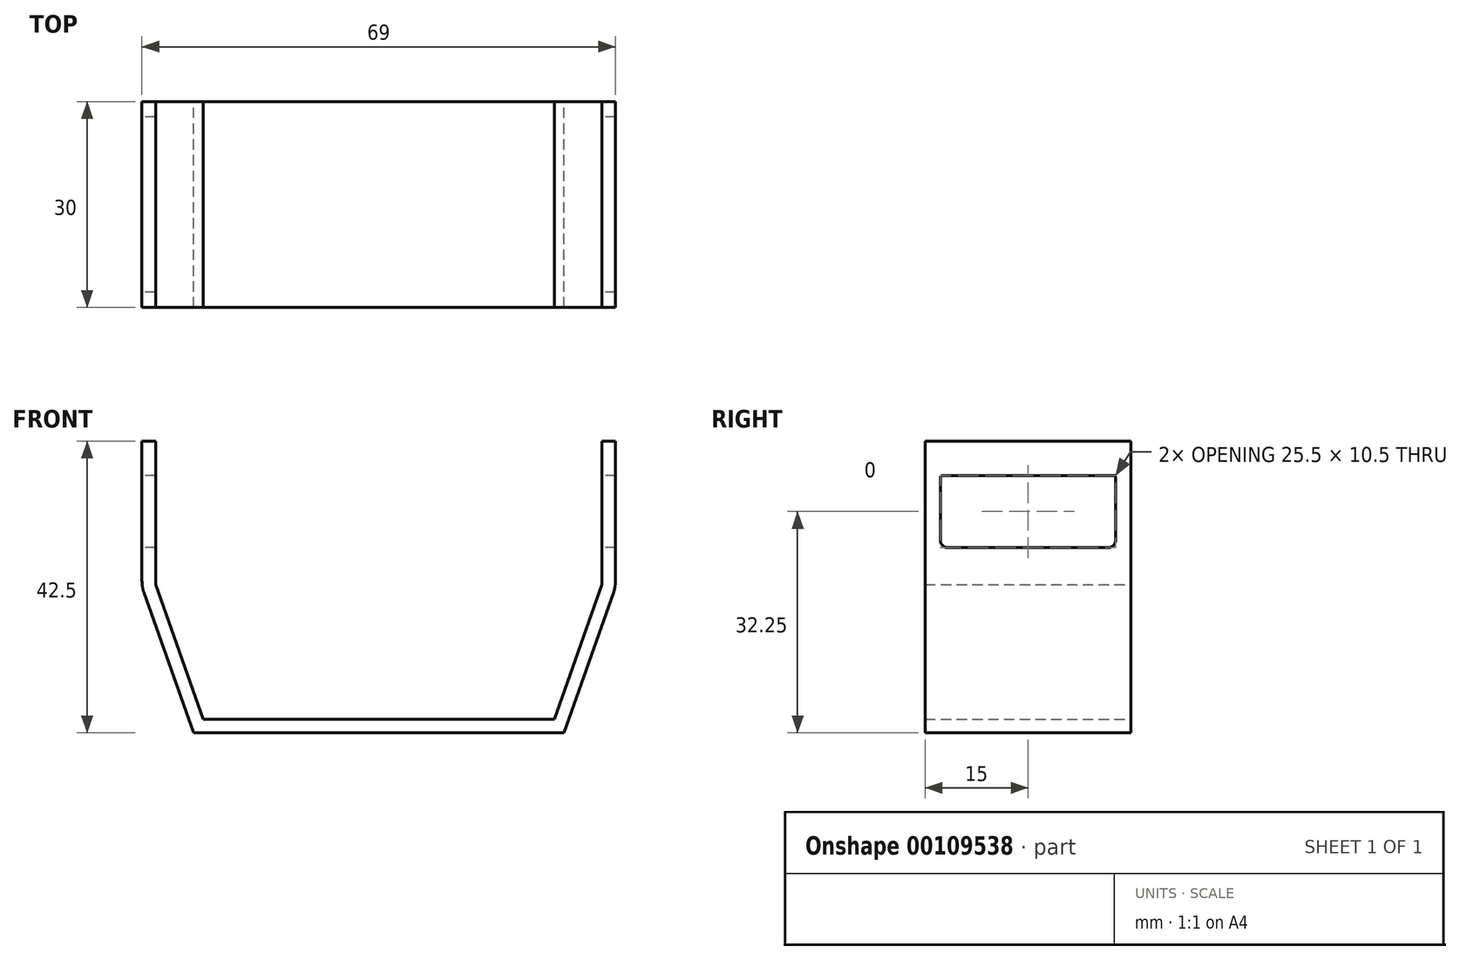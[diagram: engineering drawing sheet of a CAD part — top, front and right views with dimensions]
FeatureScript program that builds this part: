
annotation { "Feature Type Name" : "Feature", "Feature Type Description" : "" }
export const myFeature = defineFeature(function(context is Context, id is Id, definition is map)
    precondition{}
    {
        {
            var Q0;
            Q0=qCreatedBy(makeId("Front.planeOp"),FACE);
            var sketch = newSketch(context, id + "F0", { "sketchPlane" : qUnion([Q0])});
            skLineSegment(sketch, "E0", {"start": v(34.5, 0) * mm, "end": v(34.5, 21.25) * mm, "construction": true});
            skLineSegment(sketch, "E1", {"start": v(0, 0) * mm, "end": v(27, 0) * mm});
            skLineSegment(sketch, "E2", {"start": v(0, 0) * mm, "end": v(0, -5.67) * mm, "construction": true});
            skLineSegment(sketch, "E3", {"start": v(0, -5.67) * mm, "end": v(34.5, -5.67) * mm, "construction": true});
            skLineSegment(sketch, "E4", {"start": v(34.5, -5.67) * mm, "end": v(34.5, 0) * mm, "construction": true});
            skLineSegment(sketch, "E5", {"start": v(27, 0) * mm, "end": v(34.21, 20.44) * mm});
            skLineSegment(sketch, "E6", {"start": v(34.5, 22.1) * mm, "end": v(34.5, 42.5) * mm});
            skPoint(sketch, "E7.visualSharp", {"position": v(34.5, 21.25) * mm});
            skArc(sketch, "E7.filletArc", {"start": v(34.21, 20.44) * mm, "mid": v(34.43, 21.26) * mm, "end": v(34.5, 22.1) * mm});
            skLineSegment(sketch, "E8.0", {"start": v(32.5, 21.6) * mm, "end": v(32.5, 42.5) * mm});
            skLineSegment(sketch, "E8.1", {"start": v(25.58, 2) * mm, "end": v(32.5, 21.6) * mm});
            skLineSegment(sketch, "E8.2", {"start": v(0, 2) * mm, "end": v(25.58, 2) * mm});
            skLineSegment(sketch, "E9", {"start": v(32.5, 42.5) * mm, "end": v(34.5, 42.5) * mm});
            skArc(sketch, "E10.MirrorCS", {"start": v(-34.21, 20.44) * mm, "mid": v(-34.43, 21.26) * mm, "end": v(-34.5, 22.1) * mm});
            skLineSegment(sketch, "E11.MirrorCS", {"start": v(-32.5, 42.5) * mm, "end": v(-34.5, 42.5) * mm});
            skPoint(sketch, "E12.MirrorP", {"position": v(-34.5, 21.25) * mm});
            skLineSegment(sketch, "E13.MirrorCS", {"start": v(-25.58, 2) * mm, "end": v(-32.5, 21.6) * mm});
            skLineSegment(sketch, "E14.MirrorCS", {"start": v(-32.5, 21.6) * mm, "end": v(-32.5, 42.5) * mm});
            skLineSegment(sketch, "E15.MirrorCS", {"start": v(-34.5, 22.1) * mm, "end": v(-34.5, 42.5) * mm});
            skLineSegment(sketch, "E16.MirrorCS", {"start": v(0, 0) * mm, "end": v(-27, 0) * mm});
            skLineSegment(sketch, "E17.MirrorCS", {"start": v(0, 2) * mm, "end": v(-25.58, 2) * mm});
            skLineSegment(sketch, "E18.MirrorCS", {"start": v(-27, 0) * mm, "end": v(-34.21, 20.44) * mm});
            skSolve(sketch);
        }
        {
            var Q0;
            Q0=qSketchRegion(id+"F0",true);
            extrude(context, id + "F1", {"entities" : qUnion([Q0]), "depth" : 30 * mm});
        }
        {
            var Q0;
            Q0=makeQuery(id+"F1.opExtrude","SWEPT_FACE",FACE,{"disambiguationData":[OSD([sQuery(id+"F0.wireOp",EDGE,"E15.MirrorCS")])]});
            var sketch = newSketch(context, id + "F2", { "sketchPlane" : qUnion([Q0])});
            skLineSegment(sketch, "E19", {"start": v(2.25, 46.44) * mm, "end": v(2.25, 37.5) * mm, "construction": true});
            skLineSegment(sketch, "E20", {"start": v(0, 37.5) * mm, "end": v(2.25, 37.5) * mm, "construction": true});
            skLineSegment(sketch, "E21", {"start": v(27.75, 46.57) * mm, "end": v(27.75, 37.5) * mm, "construction": true});
            skLineSegment(sketch, "E22", {"start": v(0, 27) * mm, "end": v(2.25, 27) * mm, "construction": true});
            skLineSegment(sketch, "E23", {"start": v(2.25, 37.25) * mm, "end": v(2.25, 28) * mm});
            skLineSegment(sketch, "E24", {"start": v(3.25, 27) * mm, "end": v(26.75, 27) * mm});
            skLineSegment(sketch, "E25", {"start": v(27.75, 28) * mm, "end": v(27.75, 37.25) * mm});
            skLineSegment(sketch, "E26", {"start": v(27.5, 37.5) * mm, "end": v(2.5, 37.5) * mm});
            skLineSegment(sketch, "E27.trimOffspring", {"start": v(27.75, 37.5) * mm, "end": v(30, 37.5) * mm, "construction": true});
            skLineSegment(sketch, "E28.trimOffspring", {"start": v(27.75, 27) * mm, "end": v(27.75, 19.94) * mm, "construction": true});
            skLineSegment(sketch, "E29.trimOffspring", {"start": v(27.75, 27) * mm, "end": v(30, 27) * mm, "construction": true});
            skLineSegment(sketch, "E30.trimOffspring", {"start": v(2.25, 27) * mm, "end": v(2.25, 19.82) * mm, "construction": true});
            skPoint(sketch, "E31.visualSharp", {"position": v(27.75, 37.5) * mm});
            skArc(sketch, "E31.filletArc", {"start": v(27.75, 37.25) * mm, "mid": v(27.68, 37.43) * mm, "end": v(27.5, 37.5) * mm});
            skPoint(sketch, "E32.visualSharp", {"position": v(27.75, 27) * mm});
            skArc(sketch, "E32.filletArc", {"start": v(26.75, 27) * mm, "mid": v(27.46, 27.3) * mm, "end": v(27.75, 28) * mm});
            skPoint(sketch, "E33.visualSharp", {"position": v(2.25, 27) * mm});
            skArc(sketch, "E33.filletArc", {"start": v(2.25, 28) * mm, "mid": v(2.54, 27.3) * mm, "end": v(3.25, 27) * mm});
            skPoint(sketch, "E34.visualSharp", {"position": v(2.25, 37.5) * mm});
            skArc(sketch, "E34.filletArc", {"start": v(2.5, 37.5) * mm, "mid": v(2.32, 37.43) * mm, "end": v(2.25, 37.25) * mm});
            skSolve(sketch);
        }
        {
            var Q0;
            Q0=qSketchRegion(id+"F2",true);
            extrude(context, id + "F3", {"entities" : qUnion([Q0]), "operationType" : NewBodyOperationType.REMOVE, "oppositeDirection" : true, "depth" : 70 * mm});
        }
    });
